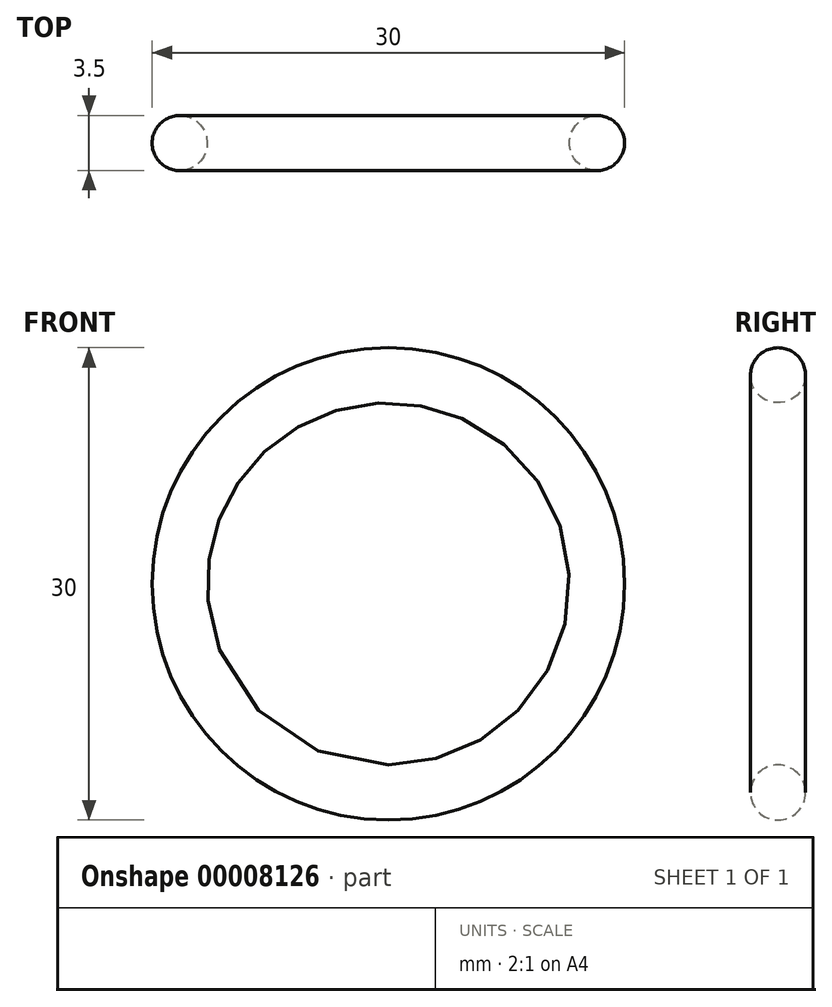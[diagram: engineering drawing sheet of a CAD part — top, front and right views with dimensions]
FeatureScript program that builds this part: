
annotation { "Feature Type Name" : "Feature", "Feature Type Description" : "" }
export const myFeature = defineFeature(function(context is Context, id is Id, definition is map)
    precondition{}
    {
        {
            var Q0;
            Q0=qCreatedBy(makeId("Top.planeOp"),FACE);
            var sketch = newSketch(context, id + "F0", { "sketchPlane" : qUnion([Q0])});
            skLineSegment(sketch, "E0", {"start": v(0, 0) * mm, "end": v(0, 10.52) * mm, "construction": true});
            skLineSegment(sketch, "E1", {"start": v(0, 0) * mm, "end": v(13.25, 0) * mm, "construction": true});
            skCircle(sketch, "E2", {"center": v(13.25, 0) * mm, "radius": 1.75 * mm});
            skLineSegment(sketch, "E3", {"start": v(15, 0) * mm, "end": v(15, -8.7) * mm, "construction": true});
            skSolve(sketch);
        }
        {
            var Q0;
            Q0 = qSketchRegion(id + "F0", true);
            var Q1;
            Q1=sQuery(id+"F0.wireOp",EDGE,"E0");
            revolve(context, id + "F1", {"entities" : qUnion([Q0]), "axis" : qUnion([Q1]), "revolveType" : RevolveType.FULL});
        }
    });
